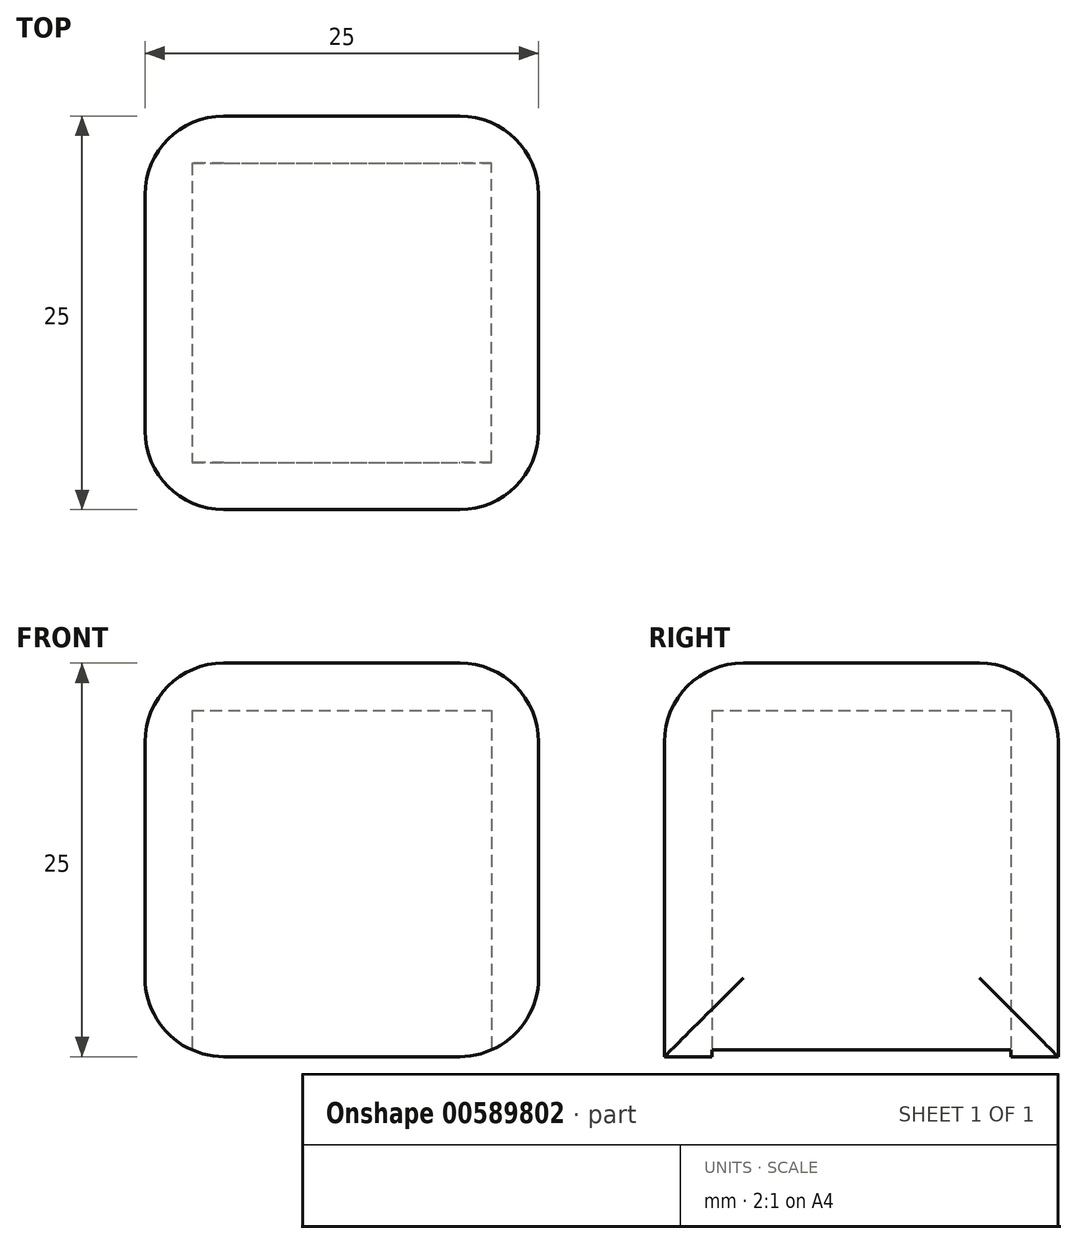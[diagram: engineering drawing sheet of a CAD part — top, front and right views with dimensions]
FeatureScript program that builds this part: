
annotation { "Feature Type Name" : "Feature", "Feature Type Description" : "" }
export const myFeature = defineFeature(function(context is Context, id is Id, definition is map)
    precondition{}
    {
        {
            var Q0;
            Q0=qCreatedBy(makeId("Top.planeOp"),FACE);
            var sketch = newSketch(context, id + "F0", { "sketchPlane" : qUnion([Q0])});
            skLineSegment(sketch, "E0.bottom", {"start": v(0, 0) * mm, "end": v(25, 0) * mm});
            skLineSegment(sketch, "E0.top", {"start": v(0, 25) * mm, "end": v(25, 25) * mm});
            skLineSegment(sketch, "E0.left", {"start": v(0, 0) * mm, "end": v(0, 25) * mm});
            skLineSegment(sketch, "E0.right", {"start": v(25, 0) * mm, "end": v(25, 25) * mm});
            skSolve(sketch);
        }
        {
            var Q0;
            Q0 = qSketchRegion(id + "F0", true);
            extrude(context, id + "F1", {"entities" : qUnion([Q0]), "depth" : 25 * mm, "offsetDistance" : 25 * mm});
        }
        {
            var Q0;
            Q0=makeQuery(id+"F1.opExtrude","CAP_FACE",FACE,{"disambiguationData":[OSD([sQuery(id+"F0.wireOp",EDGE,"E0.bottom"),sQuery(id+"F0.wireOp",EDGE,"E0.top"),sQuery(id+"F0.wireOp",EDGE,"E0.left"),sQuery(id+"F0.wireOp",EDGE,"E0.right")])],"isStart":true});
            shell(context, id + "F2", {"entities" : qUnion([Q0]), "thickness" : 3 * mm});
        }
        {
            var Q0;
            Q0=makeQuery(id+"F1.opExtrude","SWEPT_EDGE",EDGE,{"disambiguationData":[OSD([sQuery(id+"F0.wireOp",EDGE,"E0.top"),sQuery(id+"F0.wireOp",EDGE,"E0.right")])]});
            var Q1;
            Q1=makeQuery(id+"F1.opExtrude","SWEPT_EDGE",EDGE,{"disambiguationData":[OSD([sQuery(id+"F0.wireOp",EDGE,"E0.bottom"),sQuery(id+"F0.wireOp",EDGE,"E0.right")])]});
            var Q2;
            Q2=makeQuery(id+"F1.opExtrude","SWEPT_FACE",FACE,{"disambiguationData":[OSD([sQuery(id+"F0.wireOp",EDGE,"E0.right")])]});
            var Q3;
            Q3=makeQuery(id+"F1.opExtrude","CAP_FACE",FACE,{"disambiguationData":[OSD([sQuery(id+"F0.wireOp",EDGE,"E0.bottom"),sQuery(id+"F0.wireOp",EDGE,"E0.top"),sQuery(id+"F0.wireOp",EDGE,"E0.left"),sQuery(id+"F0.wireOp",EDGE,"E0.right")])],"isStart":false});
            var Q4;
            Q4=makeQuery(id+"F1.opExtrude","SWEPT_FACE",FACE,{"disambiguationData":[OSD([sQuery(id+"F0.wireOp",EDGE,"E0.left")])]});
            fillet(context, id + "F3", {"entities" : qUnion([Q0, Q1, Q2, Q3, Q4]), "radius" : 5 * mm, "tangentPropagation" : true, "allowEdgeOverflow" : false});
        }
    });
